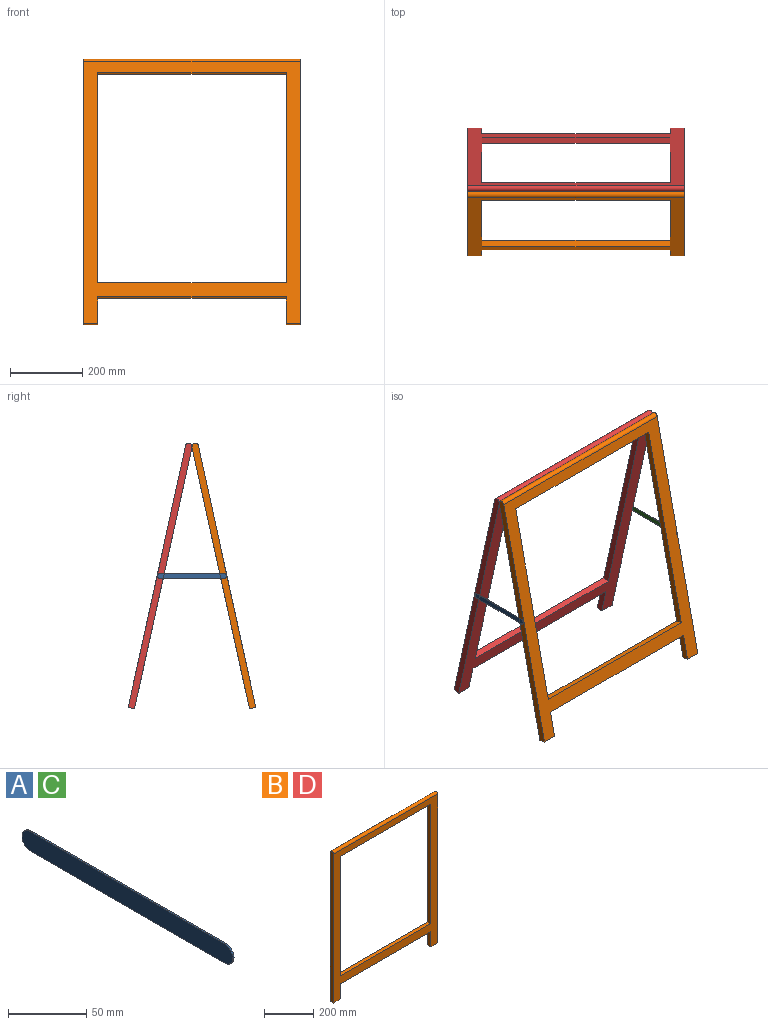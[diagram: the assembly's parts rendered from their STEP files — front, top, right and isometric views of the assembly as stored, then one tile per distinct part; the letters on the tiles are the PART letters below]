
ASSEMBLY  parts=4 mates=5
PART A: 6 faces, bbox 1.2x190x15 mm
  f0: cylinder r=7.5mm len=15mm, axis (-1,0,0), area 28.3mm2, adj f1,f3,f4,f5
  f1: plane 175x1.2mm, normal (0,0,-1), area 210mm2, adj f0,f2,f4,f5
  f2: cylinder r=7.5mm len=15mm, axis (-1,0,0), area 28.3mm2, adj f1,f3,f4,f5
  f3: plane 175x1.2mm, normal (0,0,1), area 210mm2, adj f0,f2,f4,f5
  f4: plane 190x15mm, normal (1,0,0), area 2801.7mm2, adj f0,f1,f2,f3
  f5: plane 190x15mm, normal (-1,0,0), area 2801.7mm2, adj f0,f1,f2,f3
PART B: 14 faces, bbox 600x18x750 mm
  f0: plane 750x18mm, normal (-1,0,0), area 13465.2mm2, adj f1,f11,f12,f13
  f1: plane 40x18mm, normal (0,0,-1), area 720mm2, adj f0,f2,f11,f12
  f2: plane 75x18mm, normal (1,0,0), area 1350mm2, adj f1,f3,f11,f12
  f3: plane 520x18mm, normal (0,0,-1), area 9360mm2, adj f2,f4,f11,f12
  f4: plane 75x18mm, normal (-1,0,0), area 1350mm2, adj f3,f5,f11,f12
  f5: plane 40x18mm, normal (0,0,-1), area 720mm2, adj f4,f10,f11,f12
  f6: plane 595x18mm, normal (1,0,0), area 10710mm2, adj f7,f9,f11,f12
  f7: plane 520x18mm, normal (0,0,-1), area 9360mm2, adj f6,f8,f11,f12
  f8: plane 595x18mm, normal (-1,0,0), area 10710mm2, adj f7,f9,f11,f12
  f9: plane 520x18mm, normal (0,0,1), area 9360mm2, adj f6,f8,f11,f12
  f10: plane 750x18mm, normal (1,0,0), area 13465.2mm2, adj f5,f11,f12,f13
  f11: plane 741x600mm, normal (0,-1,0), area 96200mm2, adj f0,f1,f2,f3,f4,f5,f6,f7
  f12: plane 741x600mm, normal (0,1,0), area 96200mm2, adj f0,f1,f2,f3,f4,f5,f6,f7
  f13: cylinder r=9mm len=600mm, axis (1,0,0), area 16964.6mm2, adj f0,f10,f11,f12
PART C: same geometry as A
PART D: same geometry as B
PLACE A rot(axis=(-1,0,0),0deg) t=(-601.2,36.82,-62.5)mm
PLACE B rot(axis=(-1,0,0),12.4deg) t=(-600,-246.44,-374.76)mm
PLACE C t=(0,36.82,-62.5)mm
PLACE D rot(axis=(1,0,0),12.4deg) t=(-600,89.02,-370.9)mm
MATE revolute B.f0 <-> D.f0  axis (-1,0,0) through (-600,-87.5,348.99)mm
MATE revolute C.f2 <-> D.f10  axis (-1,0,0) through (0,0,-7.5)mm
MATE revolute C.f0 <-> B.f10  axis (-1,0,0) through (0,-175,-7.5)mm
MATE revolute A.f0 <-> B.f0  axis (1,0,0) through (-600,-175,-7.5)mm
MATE revolute A.f2 <-> D.f0  axis (1,0,0) through (-600,0,-7.5)mm
